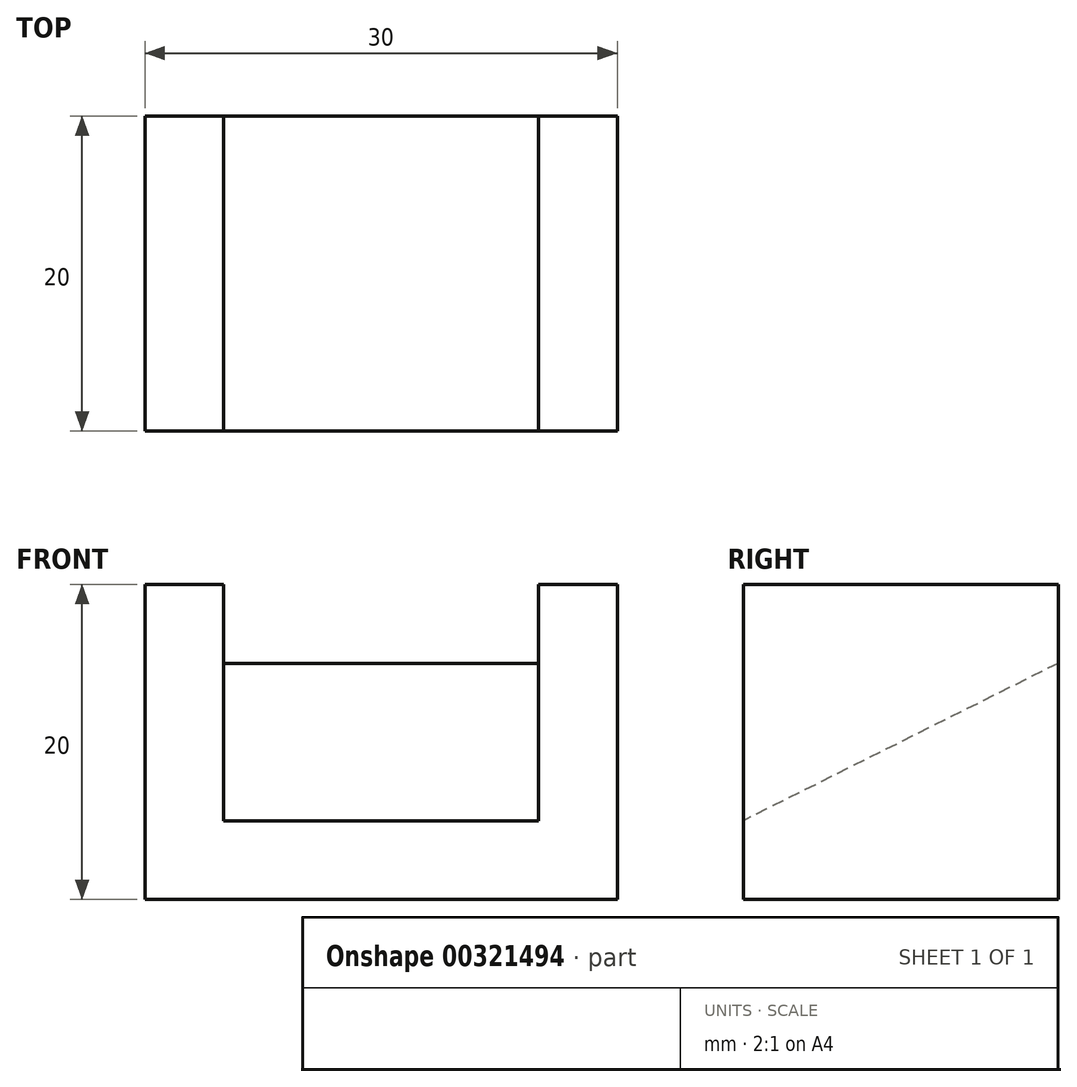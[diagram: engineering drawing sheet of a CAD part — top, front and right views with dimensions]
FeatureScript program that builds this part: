
annotation { "Feature Type Name" : "Feature", "Feature Type Description" : "" }
export const myFeature = defineFeature(function(context is Context, id is Id, definition is map)
    precondition{}
    {
        {
            var Q0;
            Q0=qCreatedBy(makeId("Right.planeOp"),FACE);
            var sketch = newSketch(context, id + "F0", { "sketchPlane" : qUnion([Q0])});
            skLineSegment(sketch, "E0.bottom", {"start": v(0, 0) * mm, "end": v(-20, 0) * mm});
            skLineSegment(sketch, "E0.top", {"start": v(0, 20) * mm, "end": v(-20, 20) * mm});
            skLineSegment(sketch, "E0.left", {"start": v(0, 0) * mm, "end": v(0, 20) * mm});
            skLineSegment(sketch, "E0.right", {"start": v(-20, 0) * mm, "end": v(-20, 20) * mm});
            skSolve(sketch);
        }
        {
            var Q0;
            Q0 = qSketchRegion(id + "F0", true);
            extrude(context, id + "F1", {"entities" : qUnion([Q0]), "oppositeDirection" : true, "depth" : 15 * mm, "hasSecondDirection" : true, "secondDirectionOppositeDirection" : false, "secondDirectionDepth" : 15 * mm});
        }
        {
            var Q0;
            Q0=qCreatedBy(makeId("Right.planeOp"),FACE);
            var sketch = newSketch(context, id + "F2", { "sketchPlane" : qUnion([Q0])});
            skLineSegment(sketch, "E1", {"start": v(0, 15) * mm, "end": v(-20, 5) * mm});
            skLineSegment(sketch, "E2", {"start": v(-20, 5) * mm, "end": v(-20, 20) * mm});
            skLineSegment(sketch, "E3", {"start": v(-20, 20) * mm, "end": v(0, 20) * mm});
            skLineSegment(sketch, "E4", {"start": v(0, 20) * mm, "end": v(0, 15) * mm});
            skSolve(sketch);
        }
        {
            var Q0;
            Q0 = qSketchRegion(id + "F2", true);
            extrude(context, id + "F3", {"entities" : qUnion([Q0]), "operationType" : NewBodyOperationType.REMOVE, "oppositeDirection" : true, "depth" : 10 * mm, "hasSecondDirection" : true, "secondDirectionOppositeDirection" : false, "secondDirectionDepth" : 10 * mm});
        }
    });
